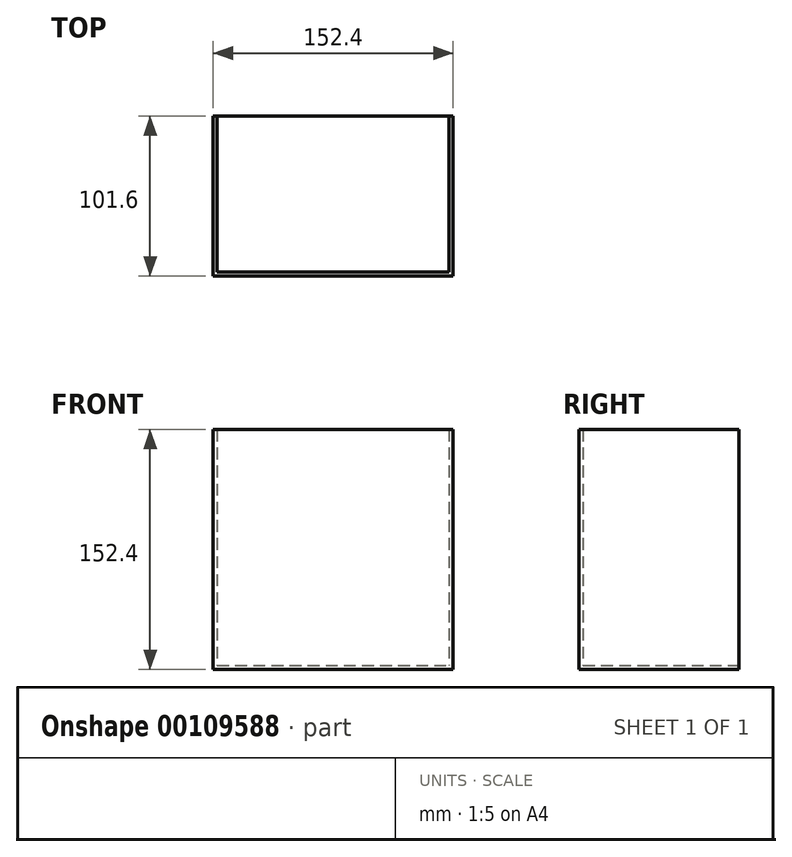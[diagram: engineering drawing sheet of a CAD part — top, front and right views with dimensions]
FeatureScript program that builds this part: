
annotation { "Feature Type Name" : "Feature", "Feature Type Description" : "" }
export const myFeature = defineFeature(function(context is Context, id is Id, definition is map)
    precondition{}
    {
        {
            var Q0;
            Q0=qCreatedBy(makeId("Front.planeOp"),FACE);
            var sketch = newSketch(context, id + "F0", { "sketchPlane" : qUnion([Q0])});
            skLineSegment(sketch, "E0.bottom", {"start": v(-76.2, 76.2) * mm, "end": v(76.2, 76.2) * mm});
            skLineSegment(sketch, "E0.top", {"start": v(-76.2, -76.2) * mm, "end": v(76.2, -76.2) * mm});
            skLineSegment(sketch, "E0.left", {"start": v(-76.2, 76.2) * mm, "end": v(-76.2, -76.2) * mm});
            skLineSegment(sketch, "E0.right", {"start": v(76.2, 76.2) * mm, "end": v(76.2, -76.2) * mm});
            skPoint(sketch, "E0.middle", {"position": v(0, 0) * mm});
            skSolve(sketch);
        }
        {
            var Q0;
            Q0 = qSketchRegion(id + "F0", true);
            extrude(context, id + "F1", {"entities" : qUnion([Q0]), "endBound" : BoundingType.SYMMETRIC, "depth" : 101.6 * mm});
        }
        {
            var Q0;
            Q0=makeQuery(id+"F1.opExtrude","CAP_FACE",FACE,{"disambiguationData":[OSD([sQuery(id+"F0.wireOp",EDGE,"E0.bottom"),sQuery(id+"F0.wireOp",EDGE,"E0.top"),sQuery(id+"F0.wireOp",EDGE,"E0.left"),sQuery(id+"F0.wireOp",EDGE,"E0.right")])],"isStart":true});
            var Q1;
            Q1=makeQuery(id+"F1.opExtrude","SWEPT_FACE",FACE,{"disambiguationData":[OSD([sQuery(id+"F0.wireOp",EDGE,"E0.bottom")])]});
            shell(context, id + "F2", {"entities" : qUnion([Q0, Q1]), "thickness" : 2.54 * mm});
        }
    });
